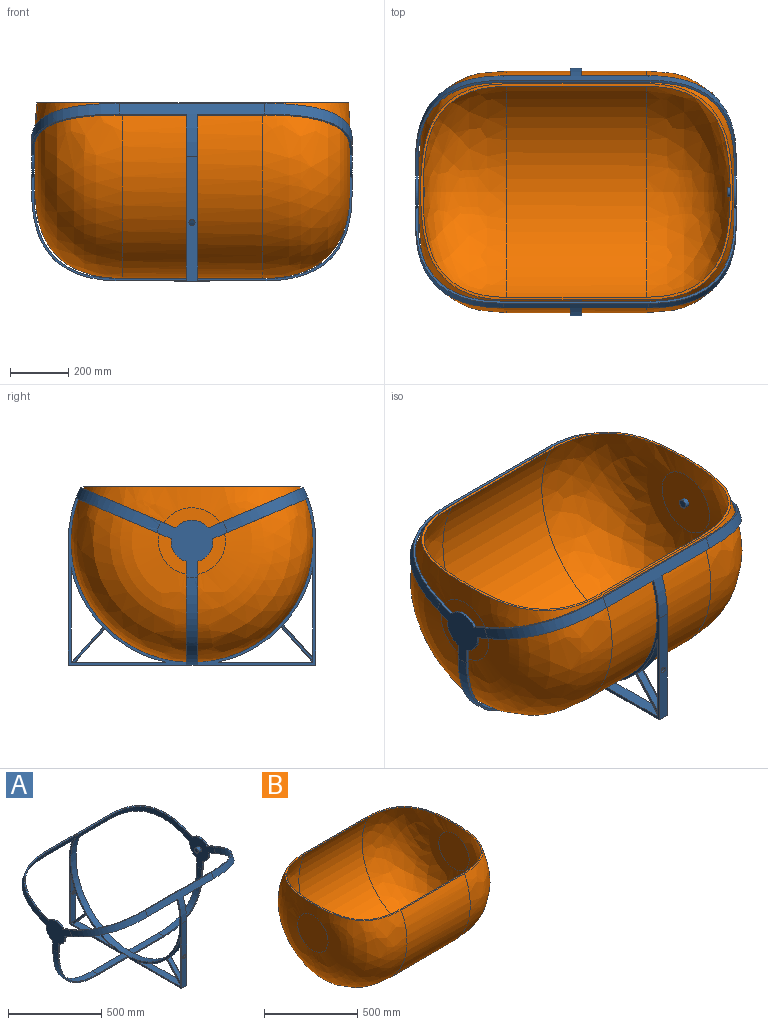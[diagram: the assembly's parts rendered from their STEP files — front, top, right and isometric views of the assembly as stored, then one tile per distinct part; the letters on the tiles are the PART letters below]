
ASSEMBLY  parts=2 mates=1
PART A: 83 faces, bbox 1116x866.2x700.2 mm
  f0: cylinder r=425mm len=323.71mm, axis (-1,0,0), area 19027.7mm2, adj f1,f49,f50,f60,f67,f68,f69,f70
  f1: plane 323.43x40mm, normal (0,0,1), area 12533.3mm2, adj f0,f49,f50,f60,f67,f68,f69,f70
  f2: cylinder r=425mm len=323.71mm, axis (-1,0,0), area 19027.2mm2, adj f3,f49,f50,f56,f63,f64,f65,f66
  f3: plane 323.71x40mm, normal (0,1,0), area 12176.2mm2, adj f2,f49,f50,f56,f58,f64,f65,f66
  f4: cylinder r=425mm len=500mm, axis (-1,0,0), area 25992.7mm2, adj f14,f32,f36,f39,f41,f49,f50,f59
  f5: cylinder r=425mm len=230mm, axis (-1,0,0), area 9208.3mm2, adj f11,f13,f43,f50
  f6: cylinder r=425mm len=500mm, axis (-1,0,0), area 25991.8mm2, adj f10,f12,f28,f38,f42,f49,f50,f52
  f7: cylinder r=417mm len=500mm, axis (-1,0,0), area 18429.4mm2, adj f14,f17,f19,f32,f36,f48,f49,f50
  f8: cylinder r=417mm len=500mm, axis (-1,0,0), area 18439.6mm2, adj f10,f12,f18,f20,f28,f49,f50,f51
  f9: cylinder r=417mm len=230mm, axis (-1,0,0), area 9208.4mm2, adj f11,f13,f24,f50
  f10: plane 530x326.93mm, normal (0,-0.39,-0.92), area 6129mm2, adj f6,f8,f20,f22,f26,f42,f44,f50
  f11: plane 530.03x355.35mm, normal (0,-1,0), area 6129.2mm2, adj f5,f9,f22,f24,f26,f43,f44,f50
  f12: plane 1100.01x326.94mm, normal (0,0.39,0.92), area 12578.8mm2, adj f6,f8,f18,f20,f21,f22,f30,f31
  f13: plane 530x355.29mm, normal (0,1,0), area 6128.9mm2, adj f5,f9,f22,f24,f33,f43,f44,f50
  f14: plane 530x326.92mm, normal (0,0.39,-0.92), area 6129mm2, adj f4,f7,f19,f22,f33,f41,f44,f50
  f15: cylinder r=15mm len=30mm, axis (-1,0,0), area 2186.6mm2, adj f22,f46
  f16: cylinder r=417mm len=230mm, axis (-1,0,0), area 9208.4mm2, adj f23,f29,f35,f49
  f17: offset ~338.87x316mm, area 18994.8mm2, adj f7,f21,f32,f36
  f18: offset ~338.87x316mm, area 18994.8mm2, adj f8,f12,f21,f28
  f19: offset ~338.87x316mm, area 18993.9mm2, adj f7,f14,f22,f32
  f20: offset ~338.87x316mm, area 18993.9mm2, adj f8,f10,f12,f22
  f21: plane 242.77x197.09mm, normal (-1,0,0), area 22007.4mm2, adj f12,f17,f18,f23,f25,f27,f28,f29
  f22: plane 242.77x197.09mm, normal (1,0,0), area 22007.3mm2, adj f10,f11,f12,f13,f14,f15,f19,f20
  f23: offset ~317.62x316mm, area 19001.3mm2, adj f16,f21,f29,f35
  f24: offset ~317.62x316mm, area 19000.3mm2, adj f9,f11,f13,f22
  f25: cylinder r=15mm len=30mm, axis (-1,0,0), area 2186.6mm2, adj f21,f53
  f26: cylinder r=72.06mm len=77.93mm, axis (1,0,0), area 813.2mm2, adj f10,f11,f22,f44
  f27: cylinder r=72.06mm len=77.93mm, axis (1,0,0), area 813.2mm2, adj f21,f28,f29,f40
  f28: plane 530x326.93mm, normal (0,-0.39,-0.92), area 6130.6mm2, adj f6,f8,f18,f21,f27,f38,f40,f49
  f29: plane 530.03x355.35mm, normal (0,-1,0), area 6130.8mm2, adj f16,f21,f23,f27,f37,f40,f45,f49
  f30: cylinder r=72.06mm len=111.74mm, axis (1,0,0), area 1022.9mm2, adj f12,f22,f32,f44
  f31: cylinder r=72.06mm len=111.74mm, axis (1,0,0), area 1022.9mm2, adj f12,f21,f32,f40
  f32: plane 1100x326.92mm, normal (0,-0.39,0.92), area 12580mm2, adj f4,f7,f17,f19,f21,f22,f30,f31
  f33: cylinder r=72.06mm len=77.94mm, axis (1,0,0), area 813.2mm2, adj f13,f14,f22,f44
  f34: cylinder r=72.06mm len=77.94mm, axis (1,0,0), area 813.2mm2, adj f21,f35,f36,f40
  f35: plane 530x355.29mm, normal (0,1,0), area 6130.4mm2, adj f16,f21,f23,f34,f37,f40,f45,f49
  f36: plane 530x326.92mm, normal (0,0.39,-0.92), area 6130.6mm2, adj f4,f7,f17,f21,f34,f39,f40,f49
  f37: bspline ~301.62x300mm, area 19504.7mm2, adj f29,f35,f40,f45
  f38: bspline ~322.87x300mm, area 19497.3mm2, adj f6,f12,f28,f40
  f39: bspline ~322.87x300mm, area 19497.3mm2, adj f4,f32,f36,f40
  f40: plane 243.1x197.08mm, normal (1,0,0), area 22714.3mm2, adj f12,f27,f28,f29,f31,f32,f34,f35
  f41: bspline ~322.87x300mm, area 19497mm2, adj f4,f14,f32,f44
  f42: bspline ~322.87x300mm, area 19497mm2, adj f6,f10,f12,f44
  f43: bspline ~301.62x300mm, area 19504.5mm2, adj f5,f11,f13,f44
  f44: plane 243.1x197.08mm, normal (-1,0,0), area 22714.4mm2, adj f10,f11,f12,f13,f14,f26,f30,f32
  f45: cylinder r=425mm len=230mm, axis (-1,0,0), area 9208.3mm2, adj f29,f35,f37,f49
  f46: plane 30x30mm, normal (1,0,0), area 706.9mm2, adj f15
  f47: cylinder r=415mm len=830mm, axis (1,0,0), area 67041.4mm2, adj f48,f49,f50,f51
  f48: plane 40x1.79mm, normal (0,-0.45,0.89), area 80mm2, adj f7,f47,f49,f50
  f49: plane 850.16x606.01mm, normal (1,0,0), area 30377.6mm2, adj f0,f1,f2,f3,f4,f6,f7,f8
  f50: plane 850.16x606.01mm, normal (-1,0,0), area 30377.6mm2, adj f0,f1,f2,f3,f4,f5,f6,f7
  f51: plane 40x1.75mm, normal (0,0.48,0.88), area 80.1mm2, adj f8,f47,f49,f50
  f52: plane 40.01x0.03mm, normal (0,0.48,0.88), area 1.2mm2, adj f6,f12
  f53: plane 30x30mm, normal (-1,0,0), area 706.9mm2, adj f25
  f54: plane 850.16x40mm, normal (0,0,-1), area 34006.4mm2, adj f49,f50,f57,f61
  f55: plane 40x0.08mm, normal (0,0,1), area 3.3mm2, adj f6,f49,f50,f57
  f56: plane 323.43x40mm, normal (0,0,1), area 12917.1mm2, adj f2,f3,f49,f50,f63,f64,f66
  f57: plane 426.37x40mm, normal (0,-1,0), area 16708.6mm2, adj f49,f50,f54,f55,f58
  f58: cylinder r=10.5mm len=21mm, axis (0,-1,0), area 659.7mm2, adj f3,f57
  f59: plane 40x0.08mm, normal (0,0,1), area 3.3mm2, adj f4,f49,f50,f61
  f60: plane 323.71x40mm, normal (0,-1,0), area 12602.1mm2, adj f0,f1,f49,f50,f62
  f61: plane 426.37x40mm, normal (0,1,0), area 16708.6mm2, adj f49,f50,f54,f59,f62
  f62: cylinder r=10.5mm len=21mm, axis (0,1,0), area 659.7mm2, adj f60,f61
  f63: plane 120.17x108.31mm, normal (0,0.74,-0.67), area 4853.2mm2, adj f2,f56,f64,f66
  f64: plane 127.47x108.98mm, normal (-1,0,0), area 1575.9mm2, adj f2,f3,f56,f63,f65
  f65: plane 113.28x102.1mm, normal (0,-0.74,0.67), area 4575.1mm2, adj f2,f3,f64,f66
  f66: plane 127.47x108.98mm, normal (1,0,0), area 1575.9mm2, adj f2,f3,f56,f63,f65
  f67: plane 120.24x108.38mm, normal (0,0.74,0.67), area 4856.2mm2, adj f0,f1,f68,f70
  f68: plane 120.24x115.41mm, normal (-1,0,0), area 1570.5mm2, adj f0,f1,f67,f69
  f69: plane 113.11x101.95mm, normal (0,-0.74,-0.67), area 4568.1mm2, adj f0,f1,f68,f70
  f70: plane 120.24x115.41mm, normal (1,0,0), area 1570.5mm2, adj f0,f1,f67,f69
  f71: plane 119.16x112.33mm, normal (-1,0,0), area 1099.3mm2, adj f72,f74,f75,f76
  f72: plane 119.16x107.4mm, normal (0,-0.74,-0.67), area 4331.3mm2, adj f71,f73,f75,f76
  f73: plane 119.16x112.33mm, normal (1,0,0), area 1099.3mm2, adj f72,f74,f75,f76
  f74: plane 114.16x102.9mm, normal (0,0.74,0.67), area 4149.8mm2, adj f71,f73,f75,f76
  f75: plane 27x9.42mm, normal (0,0,1), area 254.4mm2, adj f71,f72,f73,f74
  f76: cylinder r=425mm len=27mm, axis (-1,0,0), area 189.3mm2, adj f71,f72,f73,f74
  f77: plane 27x10.46mm, normal (0,1,0), area 282.3mm2, adj f78,f79,f80,f81
  f78: plane 124.87x107.94mm, normal (-1,0,0), area 1103.3mm2, adj f77,f79,f81,f82
  f79: plane 119.75x107.94mm, normal (0,-0.74,0.67), area 4352.9mm2, adj f77,f78,f80,f82
  f80: plane 124.87x107.94mm, normal (1,0,0), area 1103.3mm2, adj f77,f79,f81,f82
  f81: plane 114.41x103.13mm, normal (0,0.74,-0.67), area 4158.8mm2, adj f77,f78,f80,f82
  f82: cylinder r=425mm len=27mm, axis (-1,0,0), area 189.6mm2, adj f78,f79,f80,f81
PART B: 11 faces, bbox 1096x846x846 mm
  f0: plane 1070.4x741.83mm, normal (0,0,1), area 27156.3mm2, adj f1,f4,f5,f6,f9,f10
  f1: cylinder r=415mm len=830mm, axis (-1,0,0), area 811107.2mm2, adj f0,f4,f5
  f2: plane 230.01x230.01mm, normal (1,0,0), area 41544.6mm2, adj f4
  f3: plane 230.01x230.01mm, normal (-1,0,0), area 41543.9mm2, adj f5
  f4: bspline ~830x830mm, area 679315.2mm2, adj f0,f1,f2
  f5: bspline ~830x830mm, area 679317.6mm2, adj f0,f1,f3
  f6: cylinder r=407mm len=814mm, axis (-1,0,0), area 799335.1mm2, adj f0,f9,f10
  f7: plane 230x230mm, normal (-1,0,0), area 41544.6mm2, adj f9
  f8: plane 230x230mm, normal (1,0,0), area 41543.9mm2, adj f10
  f9: offset ~846x846mm, area 654619.7mm2, adj f0,f6,f7
  f10: offset ~846x846mm, area 654530.8mm2, adj f0,f6,f8
PLACE A t=(-2,0,0)mm
PLACE B at identity fixed
MATE fastened B.f1 <-> A.f30  axis (1,0,0) through (540,0,0)mm
